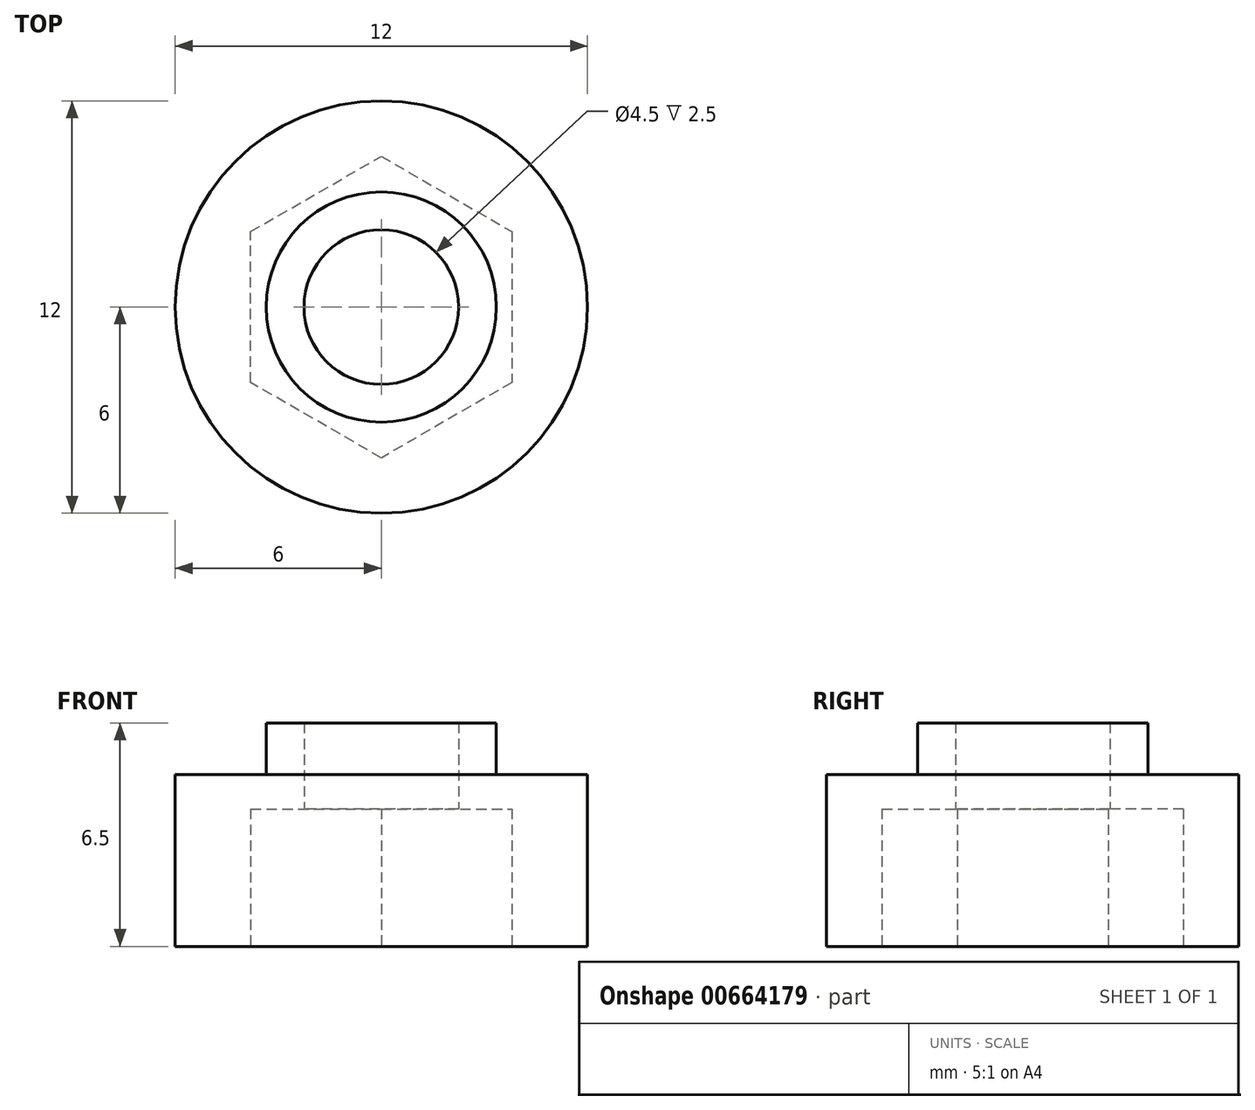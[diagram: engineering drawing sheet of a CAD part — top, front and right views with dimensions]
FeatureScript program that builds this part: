
annotation { "Feature Type Name" : "Feature", "Feature Type Description" : "" }
export const myFeature = defineFeature(function(context is Context, id is Id, definition is map)
    precondition{}
    {
        {
            var Q0;
            Q0=qCreatedBy(makeId("Top.planeOp"),FACE);
            var sketch = newSketch(context, id + "F0", { "sketchPlane" : qUnion([Q0])});
            skCircle(sketch, "E0", {"center": v(0, 0) * mm, "radius": 6 * mm});
            skCircle(sketch, "E1", {"center": v(0, 0) * mm, "radius": 3.35 * mm});
            skCircle(sketch, "E2", {"center": v(0, 0) * mm, "radius": 2.25 * mm});
            skSolve(sketch);
        }
        {
            var Q0;
            Q0=makeQuery(id+"F0.imprint","IMPRINT",FACE,{"disambiguationData":[TD([[makeQuery(id+"F0.imprint","IMPRINT",EDGE,{"derivedFrom":sQuery(id+"F0.wireOp",EDGE,"E1")}),1.0]])]});
            extrude(context, id + "F1", {"entities" : qUnion([Q0]), "depth" : 6.5 * mm, "offsetDistance" : 25 * mm});
        }
        {
            var Q0;
            Q0=makeQuery(id+"F0.imprint","IMPRINT",FACE,{"disambiguationData":[TD([[makeQuery(id+"F0.imprint","IMPRINT",EDGE,{"derivedFrom":sQuery(id+"F0.wireOp",EDGE,"E0")}),1.0]])]});
            extrude(context, id + "F2", {"entities" : qUnion([Q0]), "operationType" : NewBodyOperationType.ADD, "depth" : 5 * mm, "offsetDistance" : 25 * mm});
        }
        {
            var Q0;
            Q0=makeQuery(id+"F0.imprint","IMPRINT",FACE,{"disambiguationData":[TD([[makeQuery(id+"F0.imprint","IMPRINT",EDGE,{"derivedFrom":sQuery(id+"F0.wireOp",EDGE,"E0")}),1.0]])]});
            var sketch = newSketch(context, id + "F3", { "sketchPlane" : qUnion([Q0])});
            skCircle(sketch, "E3.cCircle", {"center": v(0, 0) * mm, "radius": 3.8 * mm, "construction": true});
            skLineSegment(sketch, "E3.0", {"start": v(0, 4.39) * mm, "end": v(3.8, 2.2) * mm});
            skLineSegment(sketch, "E3.1", {"start": v(3.8, 2.2) * mm, "end": v(3.8, -2.2) * mm});
            skLineSegment(sketch, "E3.2", {"start": v(3.8, -2.2) * mm, "end": v(0, -4.39) * mm});
            skLineSegment(sketch, "E3.3", {"start": v(0, -4.39) * mm, "end": v(-3.8, -2.2) * mm});
            skLineSegment(sketch, "E3.4", {"start": v(-3.8, -2.2) * mm, "end": v(-3.8, 2.2) * mm});
            skLineSegment(sketch, "E3.5", {"start": v(-3.8, 2.2) * mm, "end": v(0, 4.39) * mm});
            skPoint(sketch, "E3.0.midPoint", {"position": v(1.9, 3.3) * mm});
            skSolve(sketch);
        }
        {
            var Q0;
            Q0=makeQuery(id+"F3.imprint","IMPRINT",FACE,{"disambiguationData":[TD([[makeQuery(id+"F3.imprint","IMPRINT",EDGE,{"derivedFrom":sQuery(id+"F3.wireOp",EDGE,"E3.0")}),-1.0]])]});
            var Q1;
            Q1=makeQuery(id+"F0.imprint","IMPRINT",FACE,{"disambiguationData":[TD([[makeQuery(id+"F0.imprint","IMPRINT",EDGE,{"derivedFrom":sQuery(id+"F0.wireOp",EDGE,"E1")}),1.0]])]});
            extrude(context, id + "F4", {"entities" : qUnion([Q0, Q1]), "operationType" : NewBodyOperationType.REMOVE, "depth" : 4 * mm, "offsetDistance" : 25 * mm});
        }
    });
